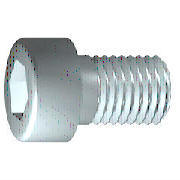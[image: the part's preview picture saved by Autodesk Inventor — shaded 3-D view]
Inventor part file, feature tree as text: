
AUTODESK INVENTOR PART (.ipt)
format: ipt  version: 2022 (Build 260153000, 153)  size: 199,168 bytes
history: native  units: mm (DEFAULTED — no unit token found)
features: sketch x2, extrude x1, plane x1, fillet x1
ambient origin geometry x7: Origin, YZ Plane, XY Plane, X Axis, Y Axis, Z Axis, Center Point
bodies: Solid1 (feature_tree), Body (feature_tree)
feature tree (5):
  extrude  "Slot"  Depth=4.0mm
  plane  "Work Plane1"
  fillet  "Fillet2"  Radius=4.0mm
  sketch  "Sketch1"  dims[d1=4.25mm d2=0.429515mm d3=4.0mm]
  sketch  "Sketch2"  dims[d4=2.0mm d5=60.0deg d6=4.0mm d7=4.0mm d8=3.464102mm d9=7.0mm d10=90.0deg d11=10.0mm d12=0.0mm d13=4.25mm d14=0.0mm d15=0.429415mm d16=0.429415mm d17=0.4mm d19=0.0mm d26=6.0mm d27=45.0deg d28=0.0mm d29=0.0mm d30=0.1mm]
